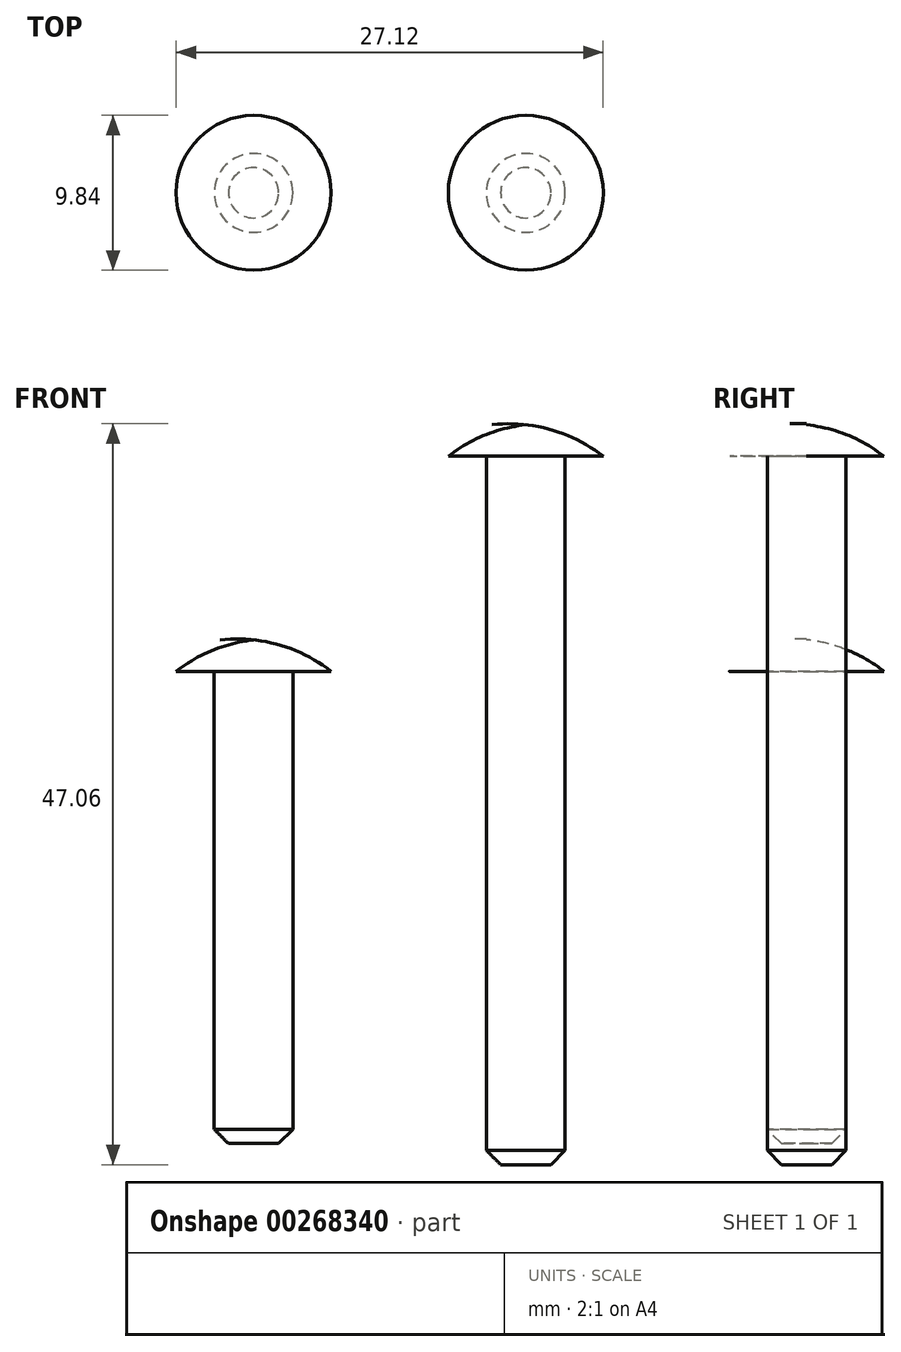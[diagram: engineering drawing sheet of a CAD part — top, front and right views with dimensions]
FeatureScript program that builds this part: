
annotation { "Feature Type Name" : "Feature", "Feature Type Description" : "" }
export const myFeature = defineFeature(function(context is Context, id is Id, definition is map)
    precondition{}
    {
        {
            var Q0;
            Q0=qCreatedBy(makeId("Front.planeOp"),FACE);
            var sketch = newSketch(context, id + "F0", { "sketchPlane" : qUnion([Q0])});
            skLineSegment(sketch, "E0", {"start": v(0, -8.06) * mm, "end": v(1.6, -8.06) * mm});
            skLineSegment(sketch, "E1", {"start": v(1.6, -8.06) * mm, "end": v(2.5, -7.16) * mm});
            skLineSegment(sketch, "E2", {"start": v(2.5, -7.16) * mm, "end": v(2.5, 21.94) * mm});
            skLineSegment(sketch, "E3", {"start": v(0, 21.94) * mm, "end": v(4.92, 21.94) * mm});
            skArc(sketch, "E4", {"start": v(4.92, 21.94) * mm, "mid": v(2.6, 23.28) * mm, "end": v(0, 23.94) * mm});
            skLineSegment(sketch, "E5", {"start": v(0, -8.06) * mm, "end": v(0, 21.94) * mm});
            skLineSegment(sketch, "E6", {"start": v(0, 21.94) * mm, "end": v(0, 23.94) * mm});
            skSolve(sketch);
        }
        {
            var Q0;
            Q0=qSketchRegion(id+"F0",true);
            var Q1;
            Q1=sQuery(id+"F0.wireOp",EDGE,"E5");
            revolve(context, id + "F1", {"entities" : qUnion([Q0]), "axis" : qUnion([Q1]), "revolveType" : RevolveType.FULL});
        }
        {
            var Q0;
            Q0=qCreatedBy(makeId("Front.planeOp"),FACE);
            var sketch = newSketch(context, id + "F2", { "sketchPlane" : qUnion([Q0])});
            skLineSegment(sketch, "E7", {"start": v(17.29, -9.4) * mm, "end": v(18.88, -9.4) * mm});
            skLineSegment(sketch, "E8", {"start": v(18.88, -9.4) * mm, "end": v(19.79, -8.5) * mm});
            skLineSegment(sketch, "E9", {"start": v(19.79, -8.5) * mm, "end": v(19.79, 35.6) * mm});
            skLineSegment(sketch, "E10", {"start": v(17.29, 35.6) * mm, "end": v(22.2, 35.6) * mm});
            skArc(sketch, "E11", {"start": v(22.2, 35.6) * mm, "mid": v(19.88, 36.94) * mm, "end": v(17.29, 37.6) * mm});
            skLineSegment(sketch, "E12", {"start": v(17.29, -9.4) * mm, "end": v(17.29, 35.6) * mm});
            skLineSegment(sketch, "E13", {"start": v(17.29, 35.6) * mm, "end": v(17.29, 37.6) * mm});
            skSolve(sketch);
        }
        {
            var Q0;
            Q0=qSketchRegion(id+"F2",true);
            var Q1;
            Q1=sQuery(id+"F2.wireOp",EDGE,"E12");
            revolve(context, id + "F3", {"entities" : qUnion([Q0]), "axis" : qUnion([Q1]), "revolveType" : RevolveType.FULL});
        }
    });
